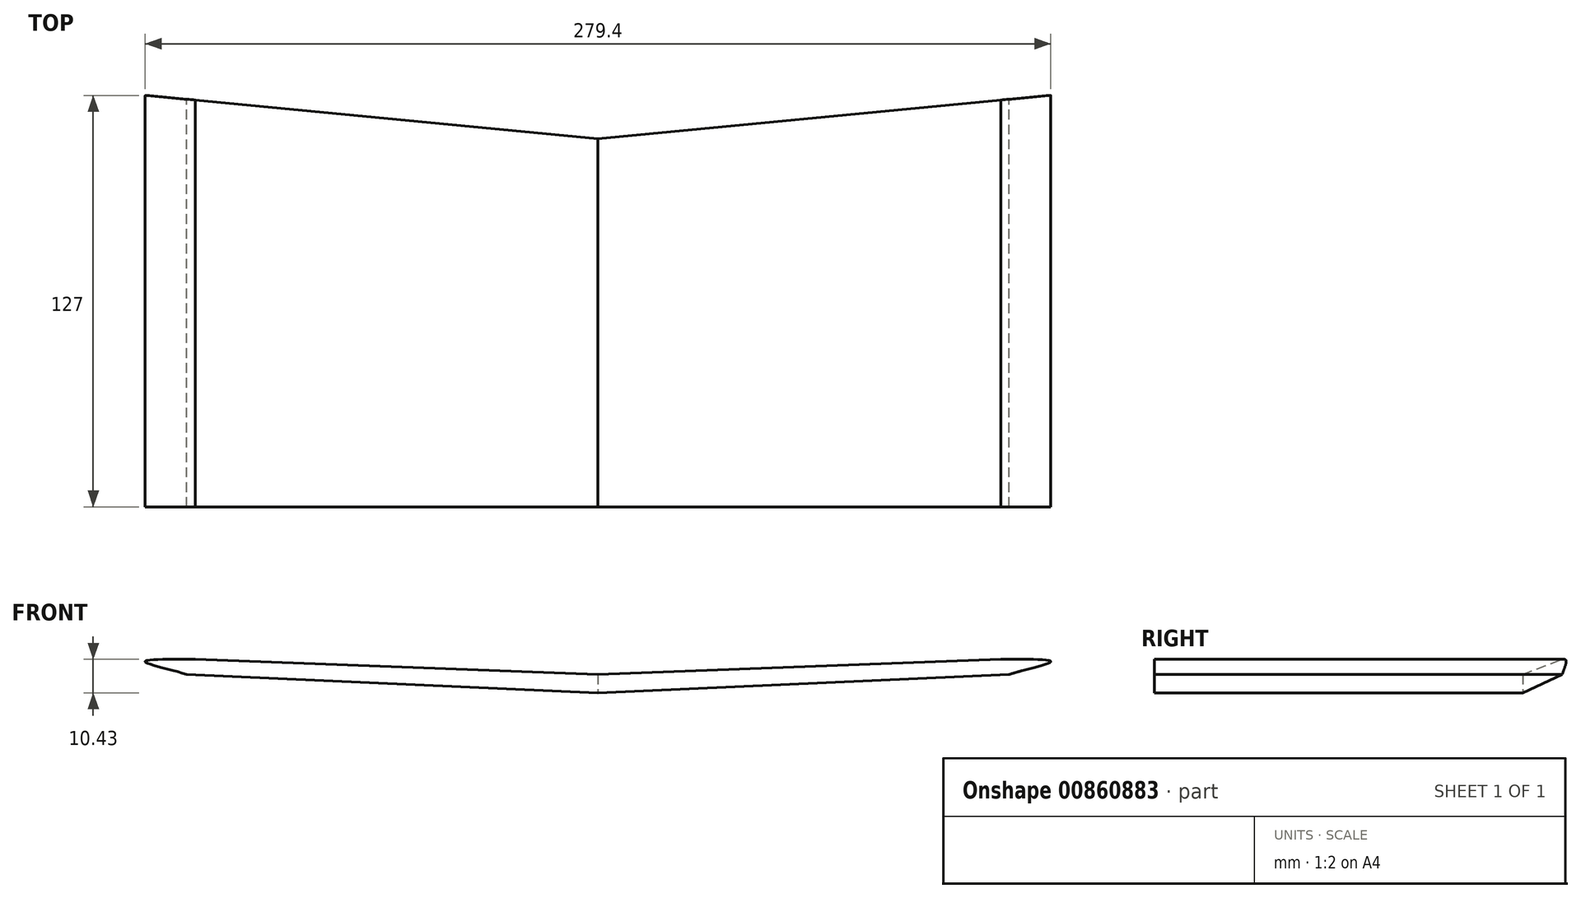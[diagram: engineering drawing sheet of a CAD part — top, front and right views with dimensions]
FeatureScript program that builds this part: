
annotation { "Feature Type Name" : "Feature", "Feature Type Description" : "" }
export const myFeature = defineFeature(function(context is Context, id is Id, definition is map)
    precondition{}
    {
        {
            var Q0;
            Q0=qCreatedBy(makeId("Front.planeOp"),FACE);
            var sketch = newSketch(context, id + "F0", { "sketchPlane" : qUnion([Q0])});
            skLineSegment(sketch, "E0", {"start": v(0, 0) * mm, "end": v(126.87, 5.71) * mm});
            skFitSpline(sketch, "E1", {"points": [v(126.87, 5.71) * mm, v(139.7, 9.71) * mm, v(124.3, 10.37) * mm], "startDerivative": vector(30.44, 10.03) * mm, "endDerivative": vector(-34.73, -0.57) * mm});
            skLineSegment(sketch, "E2", {"start": v(124.3, 10.37) * mm, "end": v(0, 5.71) * mm});
            skLineSegment(sketch, "E3.MirrorCS", {"start": v(-124.3, 10.37) * mm, "end": v(0, 5.71) * mm});
            skLineSegment(sketch, "E4.MirrorCS", {"start": v(0, 0) * mm, "end": v(-126.87, 5.71) * mm});
            skFitSpline(sketch, "E5.MirrorCS", {"points": [v(-126.87, 5.71) * mm, v(-139.7, 9.71) * mm, v(-124.3, 10.37) * mm], "startDerivative": vector(-30.44, 10.03) * mm, "endDerivative": vector(34.73, -0.57) * mm});
            skSolve(sketch);
        }
        {
            var Q0;
            Q0 = qSketchRegion(id + "F0", true);
            extrude(context, id + "F1", {"entities" : qUnion([Q0]), "depth" : 127 * mm, "offsetDistance" : 25.4 * mm});
        }
        {
            var Q0;
            Q0=qCreatedBy(makeId("Top.planeOp"),FACE);
            var sketch = newSketch(context, id + "F2", { "sketchPlane" : qUnion([Q0])});
            skLineSegment(sketch, "E6", {"start": v(-139.06, 0) * mm, "end": v(0, -13.32) * mm});
            skLineSegment(sketch, "E7.MirrorCS", {"start": v(139.06, 0) * mm, "end": v(0, -13.32) * mm});
            skLineSegment(sketch, "E8", {"start": v(-139.06, 0) * mm, "end": v(139.06, 0) * mm});
            skSolve(sketch);
        }
        {
            var Q0;
            Q0 = qSketchRegion(id + "F2", true);
            extrude(context, id + "F3", {"entities" : qUnion([Q0]), "operationType" : NewBodyOperationType.REMOVE, "depth" : 203.2 * mm, "offsetDistance" : 25.4 * mm});
        }
    });
